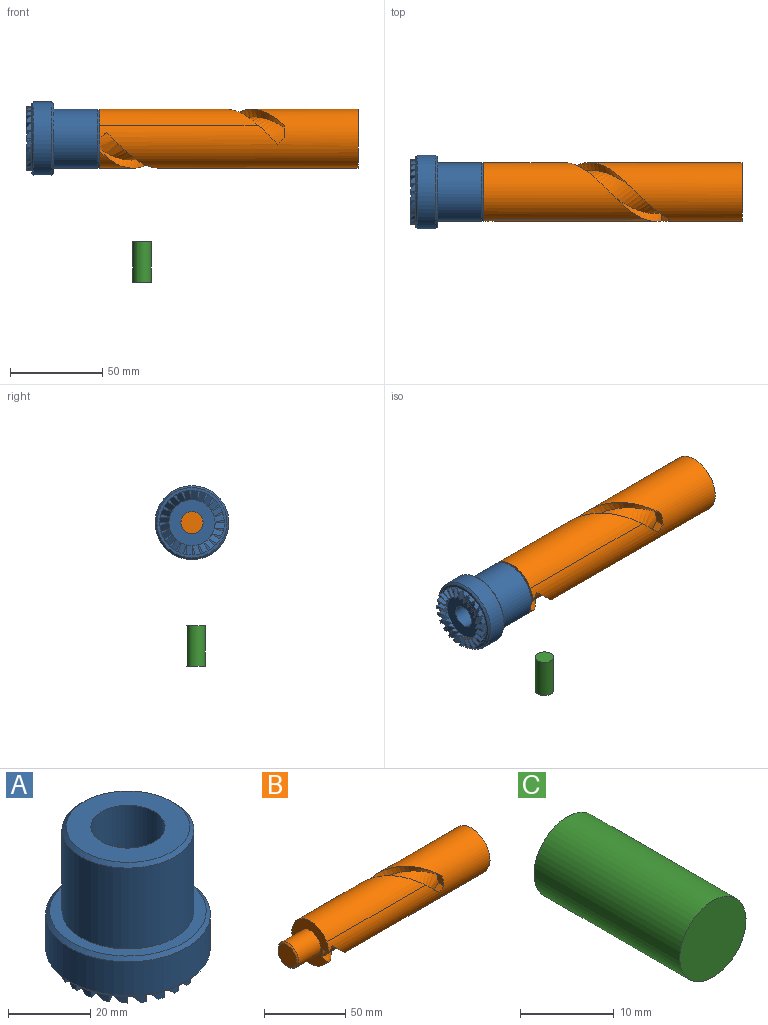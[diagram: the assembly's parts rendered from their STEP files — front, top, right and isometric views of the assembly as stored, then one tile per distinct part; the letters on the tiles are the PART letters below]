
ASSEMBLY  parts=3 mates=1
PART A: 132 faces, bbox 40x40x40 mm
  f0: cylinder r=12.5mm len=3.24mm, axis (0,0,1), area 5.3mm2, adj f46,f79,f125,f127
  f1: cylinder r=12.5mm len=3.01mm, axis (0,0,1), area 5.3mm2, adj f78,f79,f123,f124
  f2: cylinder r=12.5mm len=3mm, axis (0,0,1), area 5.3mm2, adj f68,f79,f121,f122
  f3: cylinder r=12.5mm len=3mm, axis (0,0,1), area 5.3mm2, adj f67,f79,f119,f120
  f4: cylinder r=12.5mm len=3.01mm, axis (0,0,1), area 5.3mm2, adj f66,f79,f117,f118
  f5: cylinder r=12.5mm len=3.24mm, axis (0,0,1), area 5.3mm2, adj f65,f79,f115,f116
  f6: cylinder r=12.5mm len=3.24mm, axis (0,0,1), area 5.3mm2, adj f64,f79,f113,f114
  f7: cylinder r=12.5mm len=3.01mm, axis (0,0,1), area 5.3mm2, adj f63,f79,f111,f112
  f8: cylinder r=12.5mm len=3mm, axis (0,0,1), area 5.3mm2, adj f62,f79,f109,f110
  f9: cylinder r=12.5mm len=3mm, axis (0,0,1), area 5.3mm2, adj f61,f79,f107,f108
  f10: cylinder r=12.5mm len=3.01mm, axis (0,0,1), area 5.3mm2, adj f60,f79,f105,f106
  f11: cylinder r=12.5mm len=3.24mm, axis (0,0,1), area 5.3mm2, adj f59,f79,f103,f104
  f12: cylinder r=12.5mm len=3.24mm, axis (0,0,1), area 5.3mm2, adj f58,f79,f101,f102
  f13: cylinder r=12.5mm len=3.01mm, axis (0,0,1), area 5.3mm2, adj f57,f79,f99,f100
  f14: cylinder r=12.5mm len=3mm, axis (0,0,1), area 5.3mm2, adj f56,f79,f97,f98
  f15: cylinder r=12.5mm len=3mm, axis (0,0,1), area 5.3mm2, adj f55,f79,f95,f96
  f16: cylinder r=12.5mm len=3.01mm, axis (0,0,1), area 5.3mm2, adj f54,f79,f93,f94
  f17: cylinder r=12.5mm len=3.24mm, axis (0,0,1), area 5.3mm2, adj f53,f79,f91,f92
  f18: cylinder r=12.5mm len=3.24mm, axis (0,0,1), area 5.3mm2, adj f52,f79,f89,f90
  f19: cylinder r=12.5mm len=3.01mm, axis (0,0,1), area 5.3mm2, adj f51,f79,f87,f88
  f20: cylinder r=12.5mm len=3mm, axis (0,0,1), area 5.3mm2, adj f50,f79,f85,f86
  f21: cylinder r=12.5mm len=3mm, axis (0,0,1), area 5.3mm2, adj f49,f79,f83,f84
  f22: cylinder r=12.5mm len=3.01mm, axis (0,0,1), area 5.3mm2, adj f48,f79,f81,f82
  f23: cylinder r=17.5mm len=4.53mm, axis (0,0,1), area 9.2mm2, adj f46,f74,f125,f127
  f24: cylinder r=17.5mm len=4.22mm, axis (0,0,1), area 9.2mm2, adj f74,f78,f123,f124
  f25: cylinder r=17.5mm len=3.62mm, axis (0,0,1), area 9.2mm2, adj f68,f74,f121,f122
  f26: cylinder r=17.5mm len=3.62mm, axis (0,0,1), area 9.2mm2, adj f67,f74,f119,f120
  f27: cylinder r=17.5mm len=4.22mm, axis (0,0,1), area 9.2mm2, adj f66,f74,f117,f118
  f28: cylinder r=17.5mm len=4.53mm, axis (0,0,1), area 9.2mm2, adj f65,f74,f115,f116
  f29: cylinder r=17.5mm len=4.53mm, axis (0,0,1), area 9.2mm2, adj f64,f74,f113,f114
  f30: cylinder r=17.5mm len=4.22mm, axis (0,0,1), area 9.2mm2, adj f63,f74,f111,f112
  f31: cylinder r=17.5mm len=3.62mm, axis (0,0,1), area 9.2mm2, adj f62,f74,f109,f110
  f32: cylinder r=17.5mm len=3.62mm, axis (0,0,1), area 9.2mm2, adj f61,f74,f107,f108
  f33: cylinder r=17.5mm len=4.22mm, axis (0,0,1), area 9.2mm2, adj f60,f74,f105,f106
  f34: cylinder r=17.5mm len=4.53mm, axis (0,0,1), area 9.2mm2, adj f59,f74,f103,f104
  f35: cylinder r=17.5mm len=4.53mm, axis (0,0,1), area 9.2mm2, adj f58,f74,f101,f102
  f36: cylinder r=17.5mm len=4.22mm, axis (0,0,1), area 9.2mm2, adj f57,f74,f99,f100
  f37: cylinder r=17.5mm len=3.62mm, axis (0,0,1), area 9.2mm2, adj f56,f74,f97,f98
  f38: cylinder r=17.5mm len=3.62mm, axis (0,0,1), area 9.2mm2, adj f55,f74,f95,f96
  f39: cylinder r=17.5mm len=4.22mm, axis (0,0,1), area 9.2mm2, adj f54,f74,f93,f94
  f40: cylinder r=17.5mm len=4.53mm, axis (0,0,1), area 9.2mm2, adj f53,f74,f91,f92
  f41: cylinder r=17.5mm len=4.53mm, axis (0,0,1), area 9.2mm2, adj f52,f74,f89,f90
  f42: cylinder r=17.5mm len=4.22mm, axis (0,0,1), area 9.2mm2, adj f51,f74,f87,f88
  f43: cylinder r=17.5mm len=3.62mm, axis (0,0,1), area 9.2mm2, adj f50,f74,f85,f86
  f44: cylinder r=17.5mm len=3.62mm, axis (0,0,1), area 9.2mm2, adj f49,f74,f83,f84
  f45: cylinder r=17.5mm len=4.22mm, axis (0,0,1), area 9.2mm2, adj f48,f74,f81,f82
  f46: plane 5.17x1.53mm, normal (0,0,-1), area 4.5mm2, adj f0,f23,f125,f127
  f47: plane 5x1.56mm, normal (0,0,-1), area 4.5mm2, adj f76,f77,f80,f126
  f48: plane 4.89x2.79mm, normal (0,0,-1), area 4.5mm2, adj f22,f45,f81,f82
  f49: plane 4.45x3.82mm, normal (0,0,-1), area 4.5mm2, adj f21,f44,f83,f84
  f50: plane 4.59x3.71mm, normal (0,0,-1), area 4.5mm2, adj f20,f43,f85,f86
  f51: plane 5.05x2.71mm, normal (0,0,-1), area 4.5mm2, adj f19,f42,f87,f88
  f52: plane 5.17x1.53mm, normal (0,0,-1), area 4.5mm2, adj f18,f41,f89,f90
  f53: plane 5x1.56mm, normal (0,0,-1), area 4.5mm2, adj f17,f40,f91,f92
  f54: plane 4.89x2.79mm, normal (0,0,-1), area 4.5mm2, adj f16,f39,f93,f94
  f55: plane 4.45x3.82mm, normal (0,0,-1), area 4.5mm2, adj f15,f38,f95,f96
  f56: plane 4.59x3.71mm, normal (0,0,-1), area 4.5mm2, adj f14,f37,f97,f98
  f57: plane 5.05x2.71mm, normal (0,0,-1), area 4.5mm2, adj f13,f36,f99,f100
  f58: plane 5.17x1.53mm, normal (0,0,-1), area 4.5mm2, adj f12,f35,f101,f102
  f59: plane 5x1.56mm, normal (0,0,-1), area 4.5mm2, adj f11,f34,f103,f104
  f60: plane 4.89x2.79mm, normal (0,0,-1), area 4.5mm2, adj f10,f33,f105,f106
  f61: plane 4.45x3.82mm, normal (0,0,-1), area 4.5mm2, adj f9,f32,f107,f108
  f62: plane 4.59x3.71mm, normal (0,0,-1), area 4.5mm2, adj f8,f31,f109,f110
  f63: plane 5.05x2.71mm, normal (0,0,-1), area 4.5mm2, adj f7,f30,f111,f112
  f64: plane 5.17x1.53mm, normal (0,0,-1), area 4.5mm2, adj f6,f29,f113,f114
  f65: plane 5x1.56mm, normal (0,0,-1), area 4.5mm2, adj f5,f28,f115,f116
  f66: plane 4.89x2.79mm, normal (0,0,-1), area 4.5mm2, adj f4,f27,f117,f118
  f67: plane 4.45x3.82mm, normal (0,0,-1), area 4.5mm2, adj f3,f26,f119,f120
  f68: plane 4.59x3.71mm, normal (0,0,-1), area 4.5mm2, adj f2,f25,f121,f122
  f69: cylinder r=16mm len=32mm, axis (0,0,1), area 2412.7mm2, adj f75,f129
  f70: plane 30x30mm, normal (0,0,1), area 452.4mm2, adj f71,f129
  f71: cylinder r=9mm len=20mm, axis (0,0,1), area 1131mm2, adj f70,f72
  f72: plane 18x18mm, normal (0,0,1), area 141.4mm2, adj f71,f128
  f73: cylinder r=20mm len=40mm, axis (0,0,1), area 1256.6mm2, adj f130,f131
  f74: plane 38x38mm, normal (0,0,-1), area 172mm2, adj f23,f24,f25,f26,f27,f28,f29,f30
  f75: plane 38x38mm, normal (0,0,1), area 329.9mm2, adj f69,f131
  f76: cylinder r=12.5mm len=3.24mm, axis (0,0,1), area 5.3mm2, adj f47,f79,f80,f126
  f77: cylinder r=17.5mm len=4.53mm, axis (0,0,1), area 9.2mm2, adj f47,f74,f80,f126
  f78: plane 5.05x2.71mm, normal (0,0,-1), area 4.5mm2, adj f1,f24,f123,f124
  f79: plane 25x25mm, normal (0,0,-1), area 377.8mm2, adj f0,f1,f2,f3,f4,f5,f6,f7
  f80: plane 5.37x4.3mm, normal (0.68,-0.18,-0.71), area 21.4mm2, adj f47,f76,f77,f81
  f81: plane 4.83x3mm, normal (-0.97,0.26,0), area 15mm2, adj f22,f45,f48,f80
  f82: plane 5.62x5.29mm, normal (0.61,-0.35,-0.71), area 21.4mm2, adj f22,f45,f48,f83
  f83: plane 4.33x3mm, normal (-0.87,0.5,0), area 15mm2, adj f21,f44,f49,f82
  f84: plane 5.93x5.49mm, normal (0.5,-0.5,-0.71), area 21.4mm2, adj f21,f44,f49,f85
  f85: plane 3.54x3.54mm, normal (-0.71,0.71,0), area 15mm2, adj f20,f43,f50,f84
  f86: plane 6.16x4.98mm, normal (0.35,-0.61,-0.71), area 21.4mm2, adj f20,f43,f50,f87
  f87: plane 4.33x3mm, normal (-0.5,0.87,0), area 15mm2, adj f19,f42,f51,f86
  f88: plane 5.97x4.14mm, normal (0.18,-0.68,-0.71), area 21.4mm2, adj f19,f42,f51,f89
  f89: plane 4.83x3mm, normal (-0.26,0.97,0), area 15mm2, adj f18,f41,f52,f88
  f90: plane 5.38x3.01mm, normal (0,-0.71,-0.71), area 21.4mm2, adj f18,f41,f52,f91
  f91: plane 5x3mm, normal (0,1,0), area 15mm2, adj f17,f40,f53,f90
  f92: plane 5.37x4.3mm, normal (-0.18,-0.68,-0.71), area 21.4mm2, adj f17,f40,f53,f93
  f93: plane 4.83x3mm, normal (0.26,0.97,0), area 15mm2, adj f16,f39,f54,f92
  f94: plane 5.62x5.29mm, normal (-0.35,-0.61,-0.71), area 21.4mm2, adj f16,f39,f54,f95
  f95: plane 4.33x3mm, normal (0.5,0.87,0), area 15mm2, adj f15,f38,f55,f94
  f96: plane 5.93x5.49mm, normal (-0.5,-0.5,-0.71), area 21.4mm2, adj f15,f38,f55,f97
  f97: plane 3.54x3.54mm, normal (0.71,0.71,0), area 15mm2, adj f14,f37,f56,f96
  f98: plane 6.16x4.98mm, normal (-0.61,-0.35,-0.71), area 21.4mm2, adj f14,f37,f56,f99
  f99: plane 4.33x3mm, normal (0.87,0.5,0), area 15mm2, adj f13,f36,f57,f98
  f100: plane 5.97x4.14mm, normal (-0.68,-0.18,-0.71), area 21.4mm2, adj f13,f36,f57,f101
  f101: plane 4.83x3mm, normal (0.97,0.26,0), area 15mm2, adj f12,f35,f58,f100
  f102: plane 5.38x3.01mm, normal (-0.71,0,-0.71), area 21.4mm2, adj f12,f35,f58,f103
  f103: plane 5x3mm, normal (1,0,0), area 15mm2, adj f11,f34,f59,f102
  f104: plane 5.37x4.3mm, normal (-0.68,0.18,-0.71), area 21.4mm2, adj f11,f34,f59,f105
  f105: plane 4.83x3mm, normal (0.97,-0.26,0), area 15mm2, adj f10,f33,f60,f104
  f106: plane 5.62x5.29mm, normal (-0.61,0.35,-0.71), area 21.4mm2, adj f10,f33,f60,f107
  f107: plane 4.33x3mm, normal (0.87,-0.5,0), area 15mm2, adj f9,f32,f61,f106
  f108: plane 5.93x5.49mm, normal (-0.5,0.5,-0.71), area 21.4mm2, adj f9,f32,f61,f109
  f109: plane 3.54x3.54mm, normal (0.71,-0.71,0), area 15mm2, adj f8,f31,f62,f108
  f110: plane 6.16x4.98mm, normal (-0.35,0.61,-0.71), area 21.4mm2, adj f8,f31,f62,f111
  f111: plane 4.33x3mm, normal (0.5,-0.87,0), area 15mm2, adj f7,f30,f63,f110
  f112: plane 5.97x4.14mm, normal (-0.18,0.68,-0.71), area 21.4mm2, adj f7,f30,f63,f113
  f113: plane 4.83x3mm, normal (0.26,-0.97,0), area 15mm2, adj f6,f29,f64,f112
  f114: plane 5.38x3.01mm, normal (0,0.71,-0.71), area 21.4mm2, adj f6,f29,f64,f115
  f115: plane 5x3mm, normal (0,-1,0), area 15mm2, adj f5,f28,f65,f114
  f116: plane 5.37x4.3mm, normal (0.18,0.68,-0.71), area 21.4mm2, adj f5,f28,f65,f117
  f117: plane 4.83x3mm, normal (-0.26,-0.97,0), area 15mm2, adj f4,f27,f66,f116
  f118: plane 5.62x5.29mm, normal (0.35,0.61,-0.71), area 21.4mm2, adj f4,f27,f66,f119
  f119: plane 4.33x3mm, normal (-0.5,-0.87,0), area 15mm2, adj f3,f26,f67,f118
  f120: plane 5.93x5.49mm, normal (0.5,0.5,-0.71), area 21.4mm2, adj f3,f26,f67,f121
  f121: plane 3.54x3.54mm, normal (-0.71,-0.71,0), area 15mm2, adj f2,f25,f68,f120
  f122: plane 6.16x4.98mm, normal (0.61,0.35,-0.71), area 21.4mm2, adj f2,f25,f68,f123
  f123: plane 4.33x3mm, normal (-0.87,-0.5,0), area 15mm2, adj f1,f24,f78,f122
  f124: plane 5.97x4.14mm, normal (0.68,0.18,-0.71), area 21.4mm2, adj f1,f24,f78,f125
  f125: plane 4.83x3mm, normal (-0.97,-0.26,0), area 15mm2, adj f0,f23,f46,f124
  f126: plane 5x3mm, normal (-1,0,0), area 15mm2, adj f47,f76,f77,f127
  f127: plane 5.38x3.01mm, normal (0.71,0,-0.71), area 21.4mm2, adj f0,f23,f46,f126
  f128: cylinder r=6mm len=17mm, axis (0,0,-1), area 640.9mm2, adj f72,f79
  f129: cone r=15mm half-angle=45deg, axis (0,0,-1), area 137.7mm2, adj f69,f70
  f130: cone r=19mm half-angle=45deg, axis (0,0,1), area 173.3mm2, adj f73,f74
  f131: cone r=20mm half-angle=45deg, axis (0,0,-1), area 173.3mm2, adj f73,f75
PART B: 13 faces, bbox 160x43.5x43.5 mm
  f0: plane 32.04x32.04mm, normal (-1,0,0), area 518.2mm2, adj f1,f2,f5,f6,f7,f8
  f1: cylinder r=16mm len=140mm, axis (-1,0,0), area 8998.4mm2, adj f0,f2,f3,f4,f5,f6,f11,f12
  f2: cylinder r=16mm len=85.79mm, axis (-1,0,0), area 3680.8mm2, adj f0,f1,f6
  f3: plane 5.01x3.72mm, normal (-0.71,0.02,0.71), area 24.3mm2, adj f1,f6,f7,f12
  f4: bspline ~100x43.45mm, area 576.2mm2, adj f1,f5,f7,f12
  f5: plane 5x3.56mm, normal (0.71,0,-0.71), area 24.3mm2, adj f0,f1,f4,f7
  f6: bspline ~96.46x31.99mm, area 576.2mm2, adj f0,f1,f2,f3,f7
  f7: bspline ~107.07x23.5mm, area 1179.7mm2, adj f0,f3,f4,f5,f6,f12
  f8: cylinder r=9mm len=19mm, axis (1,0,0), area 1074.4mm2, adj f0,f10
  f9: plane 16x16mm, normal (-1,0,0), area 201.1mm2, adj f10
  f10: cone r=9mm half-angle=45deg, axis (1,0,0), area 75.5mm2, adj f8,f9
  f11: plane 32x32mm, normal (1,0,0), area 804.2mm2, adj f1
  f12: plane 7.01x6.24mm, normal (-1,0,0), area 31.5mm2, adj f1,f3,f4,f7
PART C: 3 faces, bbox 10x22x10 mm
  f0: cylinder r=5mm len=22mm, axis (0,1,0), area 691.2mm2, adj f1,f2
  f1: plane 10x10mm, normal (0,1,0), area 78.5mm2, adj f0
  f2: plane 10x10mm, normal (0,-1,0), area 78.5mm2, adj f0
PLACE A rot(axis=(0,1,0),90deg) t=(-16.16,8.78,-12.53)mm
PLACE B t=(-16.16,8.78,-12.53)mm
PLACE C rot(axis=(-1,0,0),90deg) t=(6.64,6.62,-101.35)mm
MATE fastened A.f71 <-> B.f8  axis (1,0,0) through (-16.16,8.78,-12.53)mm
